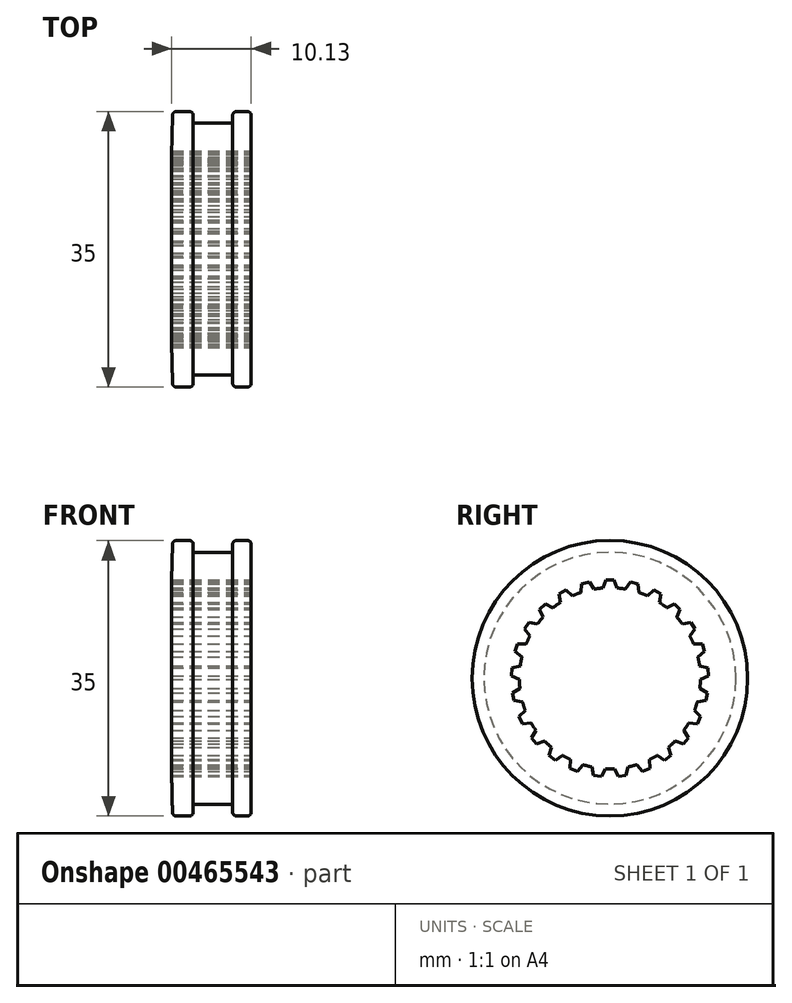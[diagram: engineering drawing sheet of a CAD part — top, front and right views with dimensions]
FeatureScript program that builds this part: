
annotation { "Feature Type Name" : "Feature", "Feature Type Description" : "" }
export const myFeature = defineFeature(function(context is Context, id is Id, definition is map)
    precondition{}
    {
        {
            var Q0;
            Q0=qCreatedBy(makeId("Front.planeOp"),FACE);
            var sketch = newSketch(context, id + "F0", { "sketchPlane" : qUnion([Q0])});
            skLineSegment(sketch, "E0", {"start": v(5, 21.27) * mm, "end": v(5, 15.77) * mm});
            skLineSegment(sketch, "E1", {"start": v(5, 15.77) * mm, "end": v(0, 15.77) * mm});
            skLineSegment(sketch, "E2", {"start": v(0, 15.77) * mm, "end": v(-5.13, 15.77) * mm});
            skLineSegment(sketch, "E3", {"start": v(-5.13, 15.77) * mm, "end": v(-5.01, 21.28) * mm});
            skLineSegment(sketch, "E4", {"start": v(-2.36, 21.27) * mm, "end": v(-2.36, 20.27) * mm});
            skLineSegment(sketch, "E5", {"start": v(-2.36, 20.27) * mm, "end": v(2.64, 20.27) * mm});
            skLineSegment(sketch, "E6", {"start": v(2.64, 20.27) * mm, "end": v(2.64, 21.27) * mm});
            skLineSegment(sketch, "E7", {"start": v(-4.51, 21.77) * mm, "end": v(-2.86, 21.77) * mm});
            skLineSegment(sketch, "E8", {"start": v(3.14, 21.77) * mm, "end": v(4.5, 21.77) * mm});
            skPoint(sketch, "E9.visualSharp", {"position": v(-2.36, 21.77) * mm});
            skArc(sketch, "E9.filletArc", {"start": v(-2.36, 21.27) * mm, "mid": v(-2.51, 21.63) * mm, "end": v(-2.86, 21.77) * mm});
            skPoint(sketch, "E10.visualSharp", {"position": v(2.64, 21.77) * mm});
            skArc(sketch, "E10.filletArc", {"start": v(3.14, 21.77) * mm, "mid": v(2.78, 21.63) * mm, "end": v(2.64, 21.27) * mm});
            skLineSegment(sketch, "E11", {"start": v(0, 15.77) * mm, "end": v(0, 4.27) * mm, "construction": true});
            skLineSegment(sketch, "E12", {"start": v(0, 4.27) * mm, "end": v(-6.31, 4.27) * mm, "construction": true});
            skPoint(sketch, "E13.visualSharp", {"position": v(-5, 21.77) * mm});
            skArc(sketch, "E13.filletArc", {"start": v(-4.51, 21.77) * mm, "mid": v(-4.86, 21.63) * mm, "end": v(-5.01, 21.28) * mm});
            skPoint(sketch, "E14.visualSharp", {"position": v(5, 21.77) * mm});
            skArc(sketch, "E14.filletArc", {"start": v(5, 21.27) * mm, "mid": v(4.85, 21.63) * mm, "end": v(4.5, 21.77) * mm});
            skSolve(sketch);
        }
        {
            var Q0;
            Q0=makeQuery(id+"F0.imprint","IMPRINT",FACE,{"disambiguationData":[TD([[makeQuery(id+"F0.imprint","IMPRINT",EDGE,{"derivedFrom":sQuery(id+"F0.wireOp",EDGE,"E0")}),-1.0]])]});
            var Q1;
            Q1=sQuery(id+"F0.wireOp",EDGE,"E12");
            revolve(context, id + "F1", {"entities" : qUnion([Q0]), "axis" : qUnion([Q1]), "revolveType" : RevolveType.FULL});
        }
        {
            var Q0;
            Q0=makeQuery(id+"F1.opRevolve","SWEPT_FACE",FACE,{"disambiguationData":[OSD([sQuery(id+"F0.wireOp",EDGE,"E0")])]});
            var sketch = newSketch(context, id + "F2", { "sketchPlane" : qUnion([Q0])});
            skLineSegment(sketch, "E15", {"start": v(0, 21.27) * mm, "end": v(0, -12.73) * mm, "construction": true});
            skLineSegment(sketch, "E16", {"start": v(0, 15.77) * mm, "end": v(0, 16.77) * mm, "construction": true});
            skLineSegment(sketch, "E17", {"start": v(0, 16.77) * mm, "end": v(0.5, 16.77) * mm});
            skLineSegment(sketch, "E18", {"start": v(0, 16.77) * mm, "end": v(-0.5, 16.77) * mm});
            skLineSegment(sketch, "E19", {"start": v(-0.5, 16.77) * mm, "end": v(-0.88, 15.74) * mm});
            skLineSegment(sketch, "E20", {"start": v(0.5, 16.77) * mm, "end": v(0.88, 15.74) * mm});
            skLineSegment(sketch, "E21", {"start": v(0, 15.77) * mm, "end": v(0, -7.23) * mm, "construction": true});
            skSolve(sketch);
        }
        {
            var Q0;
            Q0=makeQuery(id+"F2.imprint","IMPRINT",FACE,{"disambiguationData":[TD([[makeQuery(id+"F2.imprint","IMPRINT",EDGE,{"derivedFrom":sQuery(id+"F2.wireOp",EDGE,"E17")}),-1.0]])]});
            extrude(context, id + "F3", {"entities" : qUnion([Q0]), "operationType" : NewBodyOperationType.REMOVE, "oppositeDirection" : true, "depth" : 25 * mm});
        }
        {
            var Q0;
            Q0=makeQuery(id+"F3.boolean.opBoolean","COPY",FACE,{"derivedFrom":makeQuery(id+"F3.opExtrude","SWEPT_FACE",FACE,{"disambiguationData":[OSD([sQuery(id+"F2.wireOp",EDGE,"E19")])]})});
            var Q1;
            Q1=makeQuery(id+"F3.boolean.opBoolean","COPY",FACE,{"derivedFrom":makeQuery(id+"F3.opExtrude","SWEPT_FACE",FACE,{"disambiguationData":[OSD([sQuery(id+"F2.wireOp",EDGE,"E17"),sQuery(id+"F2.wireOp",EDGE,"E18")])]})});
            var Q2;
            Q2=makeQuery(id+"F3.boolean.opBoolean","COPY",FACE,{"derivedFrom":makeQuery(id+"F3.opExtrude","SWEPT_FACE",FACE,{"disambiguationData":[OSD([sQuery(id+"F2.wireOp",EDGE,"E20")])]})});
            var Q3;
            Q3=makeQuery(id+"F1.opRevolve","SWEPT_FACE",FACE,{"disambiguationData":[OSD([sQuery(id+"F0.wireOp",EDGE,"E1"),sQuery(id+"F0.wireOp",EDGE,"E2")])]});
            circularPattern(context, id + "F4", {"patternType" : PatternType.FACE, "faces" : qUnion([Q0, Q1, Q2]), "axis" : qUnion([Q3]), "angle" : 360 * degree, "instanceCount" : 25, "equalSpace" : true});
        }
    });
